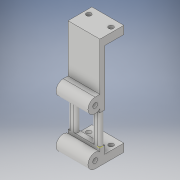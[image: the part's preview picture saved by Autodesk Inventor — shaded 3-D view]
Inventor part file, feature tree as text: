
AUTODESK INVENTOR PART (.ipt)
format: ipt  version: 2019 (Build 230136000, 136)  size: 195,584 bytes
history: native  units: mm
features: extrude x5, sketch x5, plane x1
ambient origin geometry x8: Origin, YZ Plane, XZ Plane, XY Plane, X Axis, Y Axis, Z Axis, Center Point
bodies: Solid1 (feature_tree)
feature tree (11):
  extrude  "Extrusion1"  Depth=20.0mm TaperAngle=0.0deg
  extrude  "Extrusion2"  Depth=3.0mm
  plane  "Work Plane1"
  extrude  "Extrusion3"  Depth=3.0mm
  extrude  "Extrusion4"  Depth=5.0mm
  extrude  "Extrusion5"  Depth=5.0mm
  sketch  "Sketch1"  dims[d7=3.0mm d8=20.0mm d9=0.0mm]
  sketch  "Sketch2"  dims[d10=5.0mm d11=3.0mm]
  sketch  "Sketch4"  dims[d12=5.0mm d13=3.0mm]
  sketch  "Sketch5"  dims[d14=1.5mm d15=5.0mm]
  sketch  "Sketch6"  dims[d16=3.0mm d17=5.0mm d18=3.0mm d19=1.5mm d20=19.0mm d21=0.0mm d22=19.0mm d31=3.0mm d32=20.0mm d33=0.0mm d34=12.0mm d35=20.0mm d36=12.0mm d37=20.0mm d40=3.0mm d43=3.0mm d44=5.0mm d45=0.0mm d46=12.0mm d47=20.0mm d48=12.0mm d49=20.0mm d50=3.0mm d51=3.0mm d52=5.0mm d53=0.0mm]
